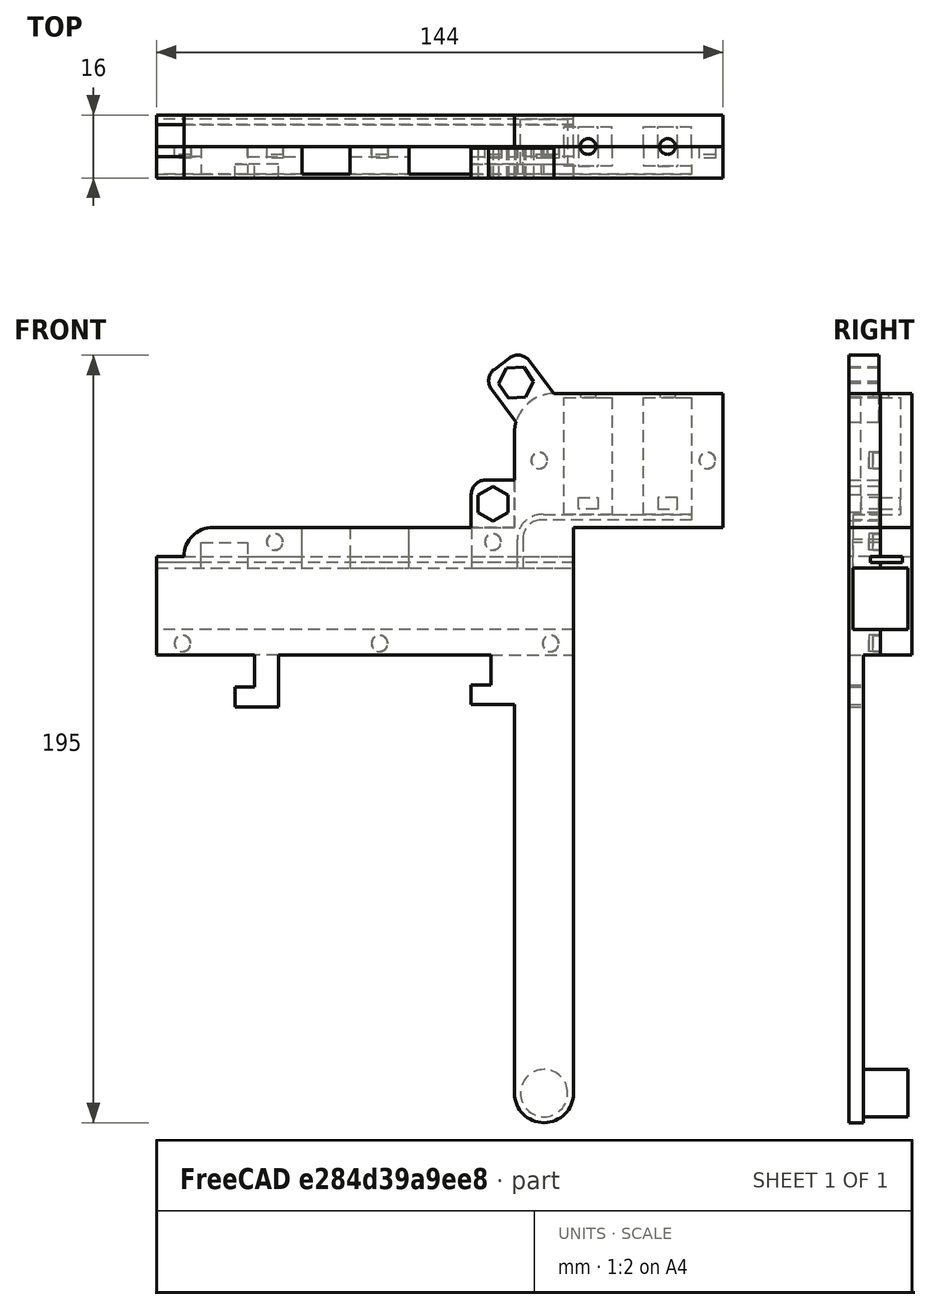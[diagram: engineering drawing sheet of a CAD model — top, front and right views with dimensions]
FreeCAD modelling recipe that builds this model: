
FCSTD DOCUMENT  (FreeCAD 0.19R24276 (Git))
Label: Feeder2
License: All rights reserved
LicenseURL: http://en.wikipedia.org/wiki/All_rights_reserved
objects: PartDesign::SubShapeBinder×35, Sketcher::SketchObject×26, PartDesign::Pocket×18, PartDesign::Pad×14, PartDesign::Hole×7, PartDesign::Body×2, Part::Refine×2, Mesh::Feature×2, Spreadsheet::Sheet×1
note: 143 computed .brp shape members not serialized (recipe doc carries the construction recipe); baked Part::Feature solids carry a one-line shape summary decoded from their .brp

FEATURE [Sketcher::SketchObject] Sketch  label="Base"
  FullyConstrained = false
  MapMode = 3
  Placement = pos=(0,0,0) rot=(1,0,0;1.5708rad)
  sketch-geometry (13):
    g0: LineSegment StartX=14.3949 StartY=7.38 StartZ=0 EndX=91 EndY=7.38 EndZ=0
    g1: LineSegment StartX=91 StartY=7.38 StartZ=0 EndX=91 EndY=31.38 EndZ=0
    g2: LineSegment StartX=0 StartY=-2.16e-14 StartZ=0 EndX=0 EndY=-25.1 EndZ=0
    g3: LineSegment StartX=0 StartY=-25.1 StartZ=0 EndX=106 EndY=-25.1 EndZ=0
    g4: LineSegment StartX=106 StartY=-25.1 StartZ=0 EndX=106 EndY=7.38 EndZ=0
    g5: LineSegment StartX=106 StartY=7.38 StartZ=0 EndX=144 EndY=7.38 EndZ=0
    g6: LineSegment StartX=144 StartY=7.38 StartZ=0 EndX=144 EndY=41.38 EndZ=0
    g7: LineSegment StartX=144 StartY=41.38 StartZ=0 EndX=101 EndY=41.38 EndZ=0
    g8: GeomPoint X=101 Y=31.38 Z=0
    g9: ArcOfCircle CenterX=101 CenterY=31.38 CenterZ=0 NormalX=0 NormalY=0 NormalZ=1 AngleXU=0 Radius=10 StartAngle=1.5708 EndAngle=3.14159
    g10: LineSegment StartX=0 StartY=-2.16e-14 StartZ=0 EndX=7 EndY=-2.16e-14 EndZ=0
    g11: GeomPoint X=14.3949 Y=-0.0149379 Z=0
    g12: ArcOfCircle CenterX=14.3949 CenterY=-0.0149379 CenterZ=0 NormalX=0 NormalY=0 NormalZ=1 AngleXU=0 Radius=7.39494 StartAngle=1.5708 EndAngle=3.13957
  constraints (37):
    c: Horizontal(g0)
    c: Coincident(g1,g0)
    c: Vertical(g1)
    c: Vertical(g2)
    c: Coincident(g3,g2)
    c: Horizontal(g3)
    c: Coincident(g4,g3)
    c: Vertical(g4)
    c: Coincident(g5,g4)
    c: Horizontal(g5)
    c: Coincident(g6,g5)
    c: Vertical(g6)
    c: Vertical(g2,g-1)
    c: Horizontal(g2,g-1)
    c: DistanceY(g2,g2) = 25.1
    c: DistanceX(g3,g3) = 106
    c: DistanceY(g4,g4) = 32.48
    c: DistanceY(g6,g6) = 34
    c: Horizontal(g0,g4)
    c: Coincident(g7,g6)
    c: Horizontal(g7)
    c: DistanceX(g7,g7) = 43
    c: DistanceY(g1,g1) = 24
    c: DistanceX(g0,g4) = 15
    c: Vertical(g8,g7)
    c: Horizontal(g1,g8)
    c: Coincident(g9,g8)
    c: Coincident(g9,g1)
    c: Coincident(g9,g7)
    c: Horizontal(g10)
    c: Horizontal(g10,g2)
    c: Vertical(g10,g2)
    c: DistanceX(g10,g10) = 7
    c: Vertical(g11,g0)
    c: Coincident(g12,g11)
    c: Coincident(g12,g10)
    c: Coincident(g12,g0)
FEATURE [PartDesign::SubShapeBinder] Binder
  BindMode = 0
  ClaimChildren = false
  Context = -> Body001 [Binder.]
  Fuse = false
  MakeFace = true
  PartialLoad = false
  Relative = true
  Support = -> [Sketch]
  _Version = 2
FEATURE [PartDesign::Pad] Pad  label="Left Base"
  Direction = (1,1,1)
  Length = 8
  Length2 = 100
  Profile = -> Binder
  Reversed = true
  Type = 0
FEATURE [Sketcher::SketchObject] Sketch001  label="ReelSupport"
  ExternalGeometry = -> [Binder]
  FullyConstrained = true
  MapMode = 5
  Placement = pos=(0,-8,1.8e-15) rot=(1,0,0;1.5708rad)
  Support = -> [Pad]
  sketch-geometry (5):
    g0: LineSegment StartX=91 StartY=-25.1 StartZ=0 EndX=106 EndY=-25.1 EndZ=0
    g1: LineSegment StartX=106 StartY=-25.1 StartZ=0 EndX=106 EndY=-136.36 EndZ=0
    g2: LineSegment StartX=91 StartY=-136.36 StartZ=0 EndX=91 EndY=-25.1 EndZ=0
    g3: GeomPoint X=98.5 Y=-136.36 Z=0
    g4: ArcOfCircle CenterX=98.5 CenterY=-136.36 CenterZ=0 NormalX=0 NormalY=0 NormalZ=1 AngleXU=0 Radius=7.5 StartAngle=3.14159 EndAngle=6.28319
  constraints (13):
    c: Coincident(g0,g1)
    c: Coincident(g2,g0)
    c: Horizontal(g0)
    c: Vertical(g1)
    c: Vertical(g2)
    c: DistanceX(g0,g0) = 15
    c: DistanceY(g1,g1) = 111.26
    c: Horizontal(g0,g-4)
    c: Vertical(g0,g-4)
    c: Symmetric(g2,g1,g3)
    c: Coincident(g4,g3)
    c: Coincident(g4,g1)
    c: Coincident(g4,g2)
FEATURE [PartDesign::Pad] Pad001  label="Reel Support"
  BaseFeature = -> Pad
  Direction = (1,1,1)
  Length = 3.6
  Length2 = 100
  Profile = -> Sketch001
  Reversed = true
  Type = 0
FEATURE [Sketcher::SketchObject] Sketch002  label="Fix1"
  ExternalGeometry = -> [Sketch001]
  FullyConstrained = true
  MapMode = 5
  Placement = pos=(0,-8,1.8e-15) rot=(1,0,0;1.5708rad)
  Support = -> [Pad001]
  sketch-geometry (6):
    g0: LineSegment StartX=91 StartY=-25.1 StartZ=0 EndX=91 EndY=-37.6 EndZ=0
    g1: LineSegment StartX=91 StartY=-37.6 StartZ=0 EndX=80 EndY=-37.6 EndZ=0
    g2: LineSegment StartX=80 StartY=-37.6 StartZ=0 EndX=80 EndY=-32.6 EndZ=0
    g3: LineSegment StartX=80 StartY=-32.6 StartZ=0 EndX=85 EndY=-32.6 EndZ=0
    g4: LineSegment StartX=85 StartY=-32.6 StartZ=0 EndX=85 EndY=-25.1 EndZ=0
    g5: LineSegment StartX=85 StartY=-25.1 StartZ=0 EndX=91 EndY=-25.1 EndZ=0
  constraints (18):
    c: Vertical(g0)
    c: Coincident(g1,g0)
    c: Horizontal(g1)
    c: Coincident(g2,g1)
    c: Vertical(g2)
    c: Coincident(g3,g2)
    c: Horizontal(g3)
    c: Coincident(g4,g3)
    c: Vertical(g4)
    c: Coincident(g5,g4)
    c: Coincident(g5,g0)
    c: Horizontal(g5)
    c: DistanceY(g2,g2) = 5
    c: DistanceX(g3,g3) = 5
    c: DistanceY(g4,g4) = 7.5
    c: DistanceX(g1,g1) = 11
    c: Horizontal(g0,g-3)
    c: Vertical(g0,g-3)
FEATURE [PartDesign::Pad] Pad002  label="Fix 1"
  BaseFeature = -> Pad001
  Direction = (1,1,1)
  Length = 3.6
  Length2 = 100
  Profile = -> Sketch002
  Reversed = true
  Type = 0
FEATURE [Sketcher::SketchObject] Sketch003  label="Fix2"
  ExternalGeometry = -> [Pad002]
  FullyConstrained = false
  MapMode = 5
  Placement = pos=(0,-8,1.8e-15) rot=(1,0,0;1.5708rad)
  Support = -> [Pad002]
  sketch-geometry (6):
    g0: LineSegment StartX=31 StartY=-38.21 StartZ=0 EndX=20 EndY=-38.21 EndZ=0
    g1: LineSegment StartX=20 StartY=-38.21 StartZ=0 EndX=20 EndY=-33.21 EndZ=0
    g2: LineSegment StartX=20 StartY=-33.21 StartZ=0 EndX=25 EndY=-33.21 EndZ=0
    g3: LineSegment StartX=25 StartY=-33.21 StartZ=0 EndX=25 EndY=-25.1 EndZ=0
    g4: LineSegment StartX=31 StartY=-38.21 StartZ=0 EndX=31 EndY=-25.1 EndZ=0
    g5: LineSegment StartX=31 StartY=-25.1 StartZ=0 EndX=25 EndY=-25.1 EndZ=0
  constraints (18):
    c: Horizontal(g0)
    c: Vertical(g1)
    c: Coincident(g2,g1)
    c: Horizontal(g2)
    c: Coincident(g3,g2)
    c: Vertical(g3)
    c: Coincident(g4,g0)
    c: Vertical(g4)
    c: Coincident(g5,g4)
    c: Coincident(g5,g3)
    c: Horizontal(g5)
    c: Equal(g1,g-3)
    c: Equal(g2,g-4)
    c: Equal(g-5,g0)
    c: Horizontal(g0,g1)
    c: Vertical(g0,g1)
    c: Horizontal(g4,g-6)
    c: DistanceX(g4,g-4) = 54
FEATURE [PartDesign::Pad] Pad003  label="Fix 2"
  BaseFeature = -> Pad002
  Direction = (1,1,1)
  Length = 3.6
  Length2 = 100
  Profile = -> Sketch003
  Reversed = true
  Type = 0
FEATURE [Sketcher::SketchObject] Sketch004  label="Hole1"
  ExternalGeometry = -> [Sketch]
  FullyConstrained = true
  MapMode = 5
  Placement = pos=(0,0,0) rot=(0,0.707107,0.707107;3.14159rad)
  Support = -> [Pad003]
  sketch-geometry (4):
    g0: LineSegment StartX=0 StartY=-2.9 StartZ=0 EndX=-106 EndY=-2.9 EndZ=0
    g1: LineSegment StartX=-106 StartY=-2.9 StartZ=0 EndX=-106 EndY=-18.6 EndZ=0
    g2: LineSegment StartX=-106 StartY=-18.6 StartZ=0 EndX=0 EndY=-18.6 EndZ=0
    g3: LineSegment StartX=0 StartY=-18.6 StartZ=0 EndX=0 EndY=-2.9 EndZ=0
  constraints (12):
    c: Coincident(g0,g1)
    c: Coincident(g1,g2)
    c: Coincident(g2,g3)
    c: Coincident(g3,g0)
    c: Horizontal(g0)
    c: Horizontal(g2)
    c: Vertical(g1)
    c: Vertical(g3)
    c: Vertical(g1,g-3)
    c: Vertical(g2,g-3)
    c: DistanceY(g-3,g1) = 6.5
    c: DistanceY(g1,g0) = 15.7
FEATURE [PartDesign::SubShapeBinder] Binder002
  BindMode = 0
  ClaimChildren = false
  Context = -> Body001 [Binder002.]
  Fuse = false
  MakeFace = true
  PartialLoad = false
  Relative = true
  Support = -> [Sketch004]
  _Version = 2
FEATURE [PartDesign::Pocket] Pocket
  BaseFeature = -> Pad003
  Length = 7
  Length2 = 100
  Profile = -> Binder002
  Type = 0
FEATURE [Sketcher::SketchObject] Sketch005  label="TapeHole"
  ExternalGeometry = -> [Sketch]
  FullyConstrained = true
  MapMode = 5
  Placement = pos=(0,0,0) rot=(1,0,0;1.5708rad)
  Support = -> [XZ_Plane001]
  expr: Constraints[8] = Spreadsheet.tape_heigh
  sketch-geometry (4):
    g0: LineSegment StartX=0 StartY=2.33e-14 StartZ=0 EndX=106 EndY=2.33e-14 EndZ=0
    g1: LineSegment StartX=106 StartY=2.33e-14 StartZ=0 EndX=106 EndY=-1.5 EndZ=0
    g2: LineSegment StartX=106 StartY=-1.5 StartZ=0 EndX=0 EndY=-1.5 EndZ=0
    g3: LineSegment StartX=0 StartY=-1.5 StartZ=0 EndX=0 EndY=2.33e-14 EndZ=0
  constraints (12):
    c: Coincident(g0,g1)
    c: Coincident(g1,g2)
    c: Coincident(g2,g3)
    c: Coincident(g3,g0)
    c: Horizontal(g0)
    c: Horizontal(g2)
    c: Vertical(g1)
    c: Vertical(g3)
    c: DistanceY(g1,g1) = 1.5
    c: Vertical(g0,g-1)
    c: Vertical(g0,g-3)
    c: Horizontal(g0,g-1)
FEATURE [PartDesign::SubShapeBinder] Binder004
  BindMode = 0
  ClaimChildren = false
  Context = -> Body001 [Binder004.]
  Fuse = false
  MakeFace = true
  PartialLoad = false
  Relative = true
  Support = -> [Sketch005]
  _Version = 2
FEATURE [PartDesign::Pocket] Pocket002
  BaseFeature = -> Pocket
  Length = 2.6
  Length2 = 100
  Profile = -> Binder004
  Type = 0
FEATURE [Sketcher::SketchObject] Sketch006  label="BoardHole1"
  ExternalGeometry = -> [Sketch]
  FullyConstrained = true
  MapMode = 5
  Placement = pos=(0,0,0) rot=(1,0,0;1.5708rad)
  Support = -> [XZ_Plane]
  sketch-geometry (4):
    g0: LineSegment StartX=11.4 StartY=3.58 StartZ=0 EndX=23.2 EndY=3.58 EndZ=0
    g1: LineSegment StartX=23.2 StartY=3.58 StartZ=0 EndX=23.2 EndY=-3.42 EndZ=0
    g2: LineSegment StartX=23.2 StartY=-3.42 StartZ=0 EndX=11.4 EndY=-3.42 EndZ=0
    g3: LineSegment StartX=11.4 StartY=-3.42 StartZ=0 EndX=11.4 EndY=3.58 EndZ=0
  constraints (12):
    c: Coincident(g0,g1)
    c: Coincident(g1,g2)
    c: Coincident(g2,g3)
    c: Coincident(g3,g0)
    c: Horizontal(g0)
    c: Horizontal(g2)
    c: Vertical(g1)
    c: Vertical(g3)
    c: DistanceY(g1,g1) = 7
    c: DistanceX(g2,g2) = 11.8
    c: DistanceX(g-1,g0) = 11.4
    c: DistanceY(g0,g-3) = 3.8
FEATURE [PartDesign::SubShapeBinder] Binder006
  BindMode = 0
  ClaimChildren = false
  Context = -> Body001 [Binder006.]
  Fuse = false
  MakeFace = true
  PartialLoad = false
  Relative = true
  Support = -> [Sketch006]
  _Version = 2
FEATURE [PartDesign::Pocket] Pocket004
  BaseFeature = -> Pocket002
  Length = 7
  Length2 = 100
  Profile = -> Binder006
  Type = 0
FEATURE [Sketcher::SketchObject] Sketch007  label="BoardHole2"
  ExternalGeometry = -> [Sketch006,Sketch]
  FullyConstrained = true
  MapMode = 5
  Placement = pos=(0,0,0) rot=(1,0,0;1.5708rad)
  Support = -> [XZ_Plane001]
  sketch-geometry (4):
    g0: LineSegment StartX=37.04 StartY=7.38 StartZ=0 EndX=49.25 EndY=7.38 EndZ=0
    g1: LineSegment StartX=49.25 StartY=7.38 StartZ=0 EndX=49.25 EndY=-3.42 EndZ=0
    g2: LineSegment StartX=49.25 StartY=-3.42 StartZ=0 EndX=37.04 EndY=-3.42 EndZ=0
    g3: LineSegment StartX=37.04 StartY=-3.42 StartZ=0 EndX=37.04 EndY=7.38 EndZ=0
  constraints (12):
    c: Coincident(g0,g1)
    c: Coincident(g1,g2)
    c: Coincident(g2,g3)
    c: Coincident(g3,g0)
    c: Horizontal(g0)
    c: Horizontal(g2)
    c: Vertical(g1)
    c: Vertical(g3)
    c: Horizontal(g0,g-4)
    c: Horizontal(g2,g-3)
    c: DistanceX(g-3,g2) = 13.84
    c: DistanceX(g2,g2) = 12.21
FEATURE [PartDesign::SubShapeBinder] Binder007
  BindMode = 0
  ClaimChildren = false
  Context = -> Body001 [Binder007.]
  Fuse = false
  MakeFace = true
  PartialLoad = false
  Relative = true
  Support = -> [Sketch007]
  _Version = 2
FEATURE [PartDesign::Pocket] Pocket005
  BaseFeature = -> Pocket004
  Length = 7
  Length2 = 100
  Profile = -> Binder007
  Type = 0
FEATURE [Sketcher::SketchObject] Sketch008  label="BoardHole3"
  ExternalGeometry = -> [Sketch,Sketch007]
  FullyConstrained = true
  MapMode = 5
  Placement = pos=(0,0,0) rot=(1,0,0;1.5708rad)
  Support = -> [XZ_Plane001]
  sketch-geometry (4):
    g0: LineSegment StartX=64.22 StartY=7.38 StartZ=0 EndX=80.07 EndY=7.38 EndZ=0
    g1: LineSegment StartX=80.07 StartY=7.38 StartZ=0 EndX=80.07 EndY=-3.42 EndZ=0
    g2: LineSegment StartX=80.07 StartY=-3.42 StartZ=0 EndX=64.22 EndY=-3.42 EndZ=0
    g3: LineSegment StartX=64.22 StartY=-3.42 StartZ=0 EndX=64.22 EndY=7.38 EndZ=0
  constraints (12):
    c: Coincident(g0,g1)
    c: Coincident(g1,g2)
    c: Coincident(g2,g3)
    c: Coincident(g3,g0)
    c: Horizontal(g0)
    c: Horizontal(g2)
    c: Vertical(g1)
    c: Vertical(g3)
    c: Horizontal(g0,g-3)
    c: Horizontal(g2,g-4)
    c: DistanceX(g-4,g2) = 14.97
    c: DistanceX(g2,g2) = 15.85
FEATURE [PartDesign::SubShapeBinder] Binder008
  BindMode = 0
  ClaimChildren = false
  Context = -> Body001 [Binder008.]
  Fuse = false
  MakeFace = true
  PartialLoad = false
  Relative = true
  Support = -> [Sketch008]
  _Version = 2
FEATURE [PartDesign::Pocket] Pocket006
  BaseFeature = -> Pocket005
  Length = 7
  Length2 = 100
  Profile = -> Binder008
  Type = 0
FEATURE [Sketcher::SketchObject] Sketch009  label="MotorHole1"
  ExternalGeometry = -> [Sketch]
  FullyConstrained = true
  MapMode = 5
  Placement = pos=(0,0,0) rot=(1,0,0;1.5708rad)
  Support = -> [XZ_Plane001]
  sketch-geometry (10):
    g0: LineSegment StartX=123.8 StartY=40.41 StartZ=0 EndX=136 EndY=40.41 EndZ=0
    g1: LineSegment StartX=136 StartY=40.41 StartZ=0 EndX=136 EndY=10.7 EndZ=0
    g2: LineSegment StartX=136 StartY=10.7 StartZ=0 EndX=123.8 EndY=10.7 EndZ=0
    g3: LineSegment StartX=123.8 StartY=10.7 StartZ=0 EndX=123.8 EndY=40.41 EndZ=0
    g4: GeomPoint X=129.9 Y=40.41 Z=0
    g5: LineSegment StartX=127.4 StartY=12.01 StartZ=0 EndX=132.4 EndY=12.01 EndZ=0
    g6: LineSegment StartX=132.4 StartY=12.01 StartZ=0 EndX=132.4 EndY=15.01 EndZ=0
    g7: LineSegment StartX=132.4 StartY=15.01 StartZ=0 EndX=127.4 EndY=15.01 EndZ=0
    g8: LineSegment StartX=127.4 StartY=15.01 StartZ=0 EndX=127.4 EndY=12.01 EndZ=0
    g9: GeomPoint X=129.9 Y=15.01 Z=0
  constraints (26):
    c: Coincident(g0,g1)
    c: Coincident(g1,g2)
    c: Coincident(g2,g3)
    c: Coincident(g3,g0)
    c: Horizontal(g0)
    c: Horizontal(g2)
    c: Vertical(g1)
    c: Vertical(g3)
    c: DistanceY(g1,g1) = 29.71
    c: DistanceX(g2,g2) = 12.2
    c: DistanceX(g1,g-3) = 8
    c: DistanceY(g-3,g1) = 3.32
    c: Symmetric(g0,g0,g4)
    c: Coincident(g5,g6)
    c: Coincident(g6,g7)
    c: Coincident(g7,g8)
    c: Coincident(g8,g5)
    c: Horizontal(g5)
    c: Horizontal(g7)
    c: Vertical(g6)
    c: Vertical(g8)
    c: DistanceX(g5,g5) = 5
    c: Symmetric(g7,g7,g9)
    c: DistanceY(g8,g8) = 3
    c: Vertical(g4,g9)
    c: DistanceY(g6,g0) = 25.4
FEATURE [PartDesign::SubShapeBinder] Binder009
  BindMode = 0
  ClaimChildren = false
  Context = -> Body001 [Binder009.]
  Fuse = false
  MakeFace = true
  PartialLoad = false
  Relative = true
  Support = -> [Sketch009]
  _Version = 2
FEATURE [PartDesign::Pocket] Pocket007  label="Motor Hole 1"
  BaseFeature = -> Pocket006
  Length = 5
  Length2 = 100
  Profile = -> Binder009
  Type = 0
FEATURE [Sketcher::SketchObject] Sketch010  label="MotorHole2"
  ExternalGeometry = -> [Sketch009]
  FullyConstrained = true
  MapMode = 5
  Placement = pos=(0,0,0) rot=(1,0,0;1.5708rad)
  Support = -> [XZ_Plane001]
  sketch-geometry (10):
    g0: LineSegment StartX=103.6 StartY=40.41 StartZ=0 EndX=115.8 EndY=40.41 EndZ=0
    g1: LineSegment StartX=115.8 StartY=40.41 StartZ=0 EndX=115.8 EndY=10.7 EndZ=0
    g2: LineSegment StartX=115.8 StartY=10.7 StartZ=0 EndX=103.6 EndY=10.7 EndZ=0
    g3: LineSegment StartX=103.6 StartY=10.7 StartZ=0 EndX=103.6 EndY=40.41 EndZ=0
    g4: GeomPoint X=109.7 Y=40.41 Z=0
    g5: LineSegment StartX=107.2 StartY=15.01 StartZ=0 EndX=112.2 EndY=15.01 EndZ=0
    g6: LineSegment StartX=112.2 StartY=15.01 StartZ=0 EndX=112.2 EndY=12.01 EndZ=0
    g7: LineSegment StartX=112.2 StartY=12.01 StartZ=0 EndX=107.2 EndY=12.01 EndZ=0
    g8: LineSegment StartX=107.2 StartY=12.01 StartZ=0 EndX=107.2 EndY=15.01 EndZ=0
    g9: GeomPoint X=109.7 Y=15.01 Z=0
  constraints (26):
    c: Coincident(g0,g1)
    c: Coincident(g1,g2)
    c: Coincident(g2,g3)
    c: Coincident(g3,g0)
    c: Horizontal(g0)
    c: Horizontal(g2)
    c: Vertical(g1)
    c: Vertical(g3)
    c: Horizontal(g0,g-3)
    c: Horizontal(g1,g-3)
    c: DistanceX(g1,g-3) = 8
    c: Equal(g2,g-4)
    c: Symmetric(g0,g0,g4)
    c: Coincident(g5,g6)
    c: Coincident(g6,g7)
    c: Coincident(g7,g8)
    c: Coincident(g8,g5)
    c: Horizontal(g5)
    c: Horizontal(g7)
    c: Vertical(g6)
    c: Vertical(g8)
    c: Equal(g8,g-6)
    c: Equal(g5,g-5)
    c: Horizontal(g5,g-6)
    c: Symmetric(g5,g5,g9)
    c: Vertical(g9,g4)
FEATURE [PartDesign::SubShapeBinder] Binder010
  BindMode = 0
  ClaimChildren = false
  Context = -> Body001 [Binder010.]
  Fuse = false
  MakeFace = true
  PartialLoad = false
  Relative = true
  Support = -> [Sketch010]
  _Version = 2
FEATURE [PartDesign::Pocket] Pocket008  label="Motor Hole 2"
  BaseFeature = -> Pocket007
  Length = 5
  Length2 = 100
  Profile = -> Binder010
  Type = 0
FEATURE [Sketcher::SketchObject] Sketch011  label="CableMotorHole"
  ExternalGeometry = -> [Sketch009,Sketch008]
  FullyConstrained = false
  MapMode = 5
  Placement = pos=(0,0,0) rot=(1,0,0;1.5708rad)
  Support = -> [XZ_Plane001]
  sketch-geometry (8):
    g0: LineSegment StartX=98.3615 StartY=10.7 StartZ=0 EndX=136 EndY=10.7 EndZ=0
    g1: LineSegment StartX=136 StartY=10.7 StartZ=0 EndX=136 EndY=9.3 EndZ=0
    g2: LineSegment StartX=136 StartY=9.3 StartZ=0 EndX=97.7369 EndY=9.3 EndZ=0
    g3: LineSegment StartX=93.1357 StartY=4.24091 StartZ=0 EndX=93.1357 EndY=-3.42 EndZ=0
    g4: LineSegment StartX=93.1357 StartY=-3.42 StartZ=0 EndX=91.7357 EndY=-3.42 EndZ=0
    g5: LineSegment StartX=91.7357 StartY=-3.42 StartZ=0 EndX=91.7357 EndY=4.24091 EndZ=0
    g6: ArcOfCircle CenterX=98.0352 CenterY=4.40679 CenterZ=0 NormalX=0 NormalY=0 NormalZ=1 AngleXU=0 Radius=4.90229 StartAngle=1.63167 EndAngle=3.17544
    g7: ArcOfCircle CenterX=98.0352 CenterY=4.40679 CenterZ=0 NormalX=0 NormalY=0 NormalZ=1 AngleXU=0 Radius=6.30167 StartAngle=1.51898 EndAngle=3.16792
  constraints (25):
    c: Coincident(g0,g1)
    c: Coincident(g1,g2)
    c: Horizontal(g0)
    c: Horizontal(g2)
    c: Vertical(g1)
    c: DistanceY(g1,g1) = 1.4
    c: Vertical(g0,g-3)
    c: Horizontal(g0,g-3)
    c: Coincident(g3,g4)
    c: Coincident(g4,g5)
    c: Horizontal(g4)
    c: Vertical(g3)
    c: Vertical(g5)
    c: DistanceX(g4,g4) = 1.4
    c: Horizontal(g4,g-4)
    c: Horizontal(g6,g2)
    c: Coincident(g7,g6)
    c: Horizontal(g3,g5)
    c: Horizontal(g7,g0)
    c: Vertical(g7,g0)
    c: Vertical(g6,g2)
    c: Horizontal(g6,g3)
    c: Vertical(g6,g3)
    c: Horizontal(g7,g5)
    c: Vertical(g7,g5)
FEATURE [PartDesign::SubShapeBinder] Binder011
  BindMode = 0
  ClaimChildren = false
  Context = -> Body001 [Binder011.]
  Fuse = false
  MakeFace = true
  PartialLoad = false
  Relative = true
  Support = -> [Sketch011]
  _Version = 2
FEATURE [PartDesign::Pocket] Pocket009  label="Cable Motor Hole"
  BaseFeature = -> Pocket008
  Length = 7
  Length2 = 100
  Profile = -> Binder011
  Type = 0
FEATURE [Sketcher::SketchObject] Sketch012  label="MotorShaftHole1"
  AttachmentOffset = pos=(0,0,22) rot=(0,0,1;0rad)
  FullyConstrained = true
  MapMode = 5
  Placement = pos=(0,0,22) rot=(0,0,1;0rad)
  Support = -> [XY_Plane]
  sketch-geometry (1):
    g0: Circle CenterX=109.7 CenterY=0 CenterZ=0 NormalX=0 NormalY=0 NormalZ=1 AngleXU=0 Radius=2
  constraints (3):
    c: Radius(g0) = 2
    c: Horizontal(g0,g-1)
    c: DistanceX(g-1,g0) = 109.7
FEATURE [PartDesign::SubShapeBinder] Binder015
  BindMode = 0
  ClaimChildren = false
  Context = -> Body001 [Binder015.]
  Fuse = false
  MakeFace = true
  PartialLoad = false
  Relative = true
  Support = -> [Sketch012]
  _Version = 2
FEATURE [PartDesign::Pocket] Pocket013
  BaseFeature = -> Pocket009
  Length = 200
  Length2 = 100
  Profile = -> Binder015
  Reversed = true
  Type = 0
FEATURE [Sketcher::SketchObject] Sketch013  label="MotorShaftHole2"
  AttachmentOffset = pos=(0,0,22) rot=(0,0,1;0rad)
  FullyConstrained = true
  MapMode = 5
  Placement = pos=(0,0,22) rot=(0,0,1;0rad)
  Support = -> [XY_Plane001]
  sketch-geometry (1):
    g0: Circle CenterX=129.9 CenterY=0 CenterZ=0 NormalX=0 NormalY=0 NormalZ=1 AngleXU=0 Radius=2
  constraints (3):
    c: Radius(g0) = 2
    c: Horizontal(g0,g-1)
    c: DistanceX(g-1,g0) = 129.9
FEATURE [PartDesign::SubShapeBinder] Binder016
  BindMode = 0
  ClaimChildren = false
  Context = -> Body001 [Binder016.]
  Fuse = false
  MakeFace = true
  PartialLoad = false
  Relative = true
  Support = -> [Sketch013]
  _Version = 2
FEATURE [PartDesign::Pocket] Pocket014
  BaseFeature = -> Pocket013
  Length = 200
  Length2 = 100
  Profile = -> Binder016
  Reversed = true
  Type = 0
FEATURE [PartDesign::SubShapeBinder] Binder001
  BindMode = 0
  ClaimChildren = false
  Context = -> Body [Binder001.]
  Fuse = false
  MakeFace = true
  PartialLoad = false
  Relative = true
  Support = -> [Sketch]
  _Version = 2
FEATURE [PartDesign::Pad] Pad004  label="Right Main"
  Direction = (1,1,1)
  Length = 8
  Length2 = 100
  Profile = -> Binder001
  Type = 0
  expr: Length = Spreadsheet.tape_width
FEATURE [PartDesign::SubShapeBinder] Binder003
  BindMode = 0
  ClaimChildren = false
  Context = -> Body [Binder003.]
  Fuse = false
  MakeFace = true
  PartialLoad = false
  Relative = true
  Support = -> [Sketch004]
  _Version = 2
FEATURE [PartDesign::Pocket] Pocket001  label="Right Hole 1"
  BaseFeature = -> Pad004
  Length = 7
  Length2 = 100
  Profile = -> Binder003
  Reversed = true
  Type = 0
  expr: Length = Spreadsheet.tape_width - 1
FEATURE [PartDesign::SubShapeBinder] Binder005
  BindMode = 0
  ClaimChildren = false
  Context = -> Body [Binder005.]
  Fuse = false
  MakeFace = true
  PartialLoad = false
  Relative = true
  Support = -> [Sketch005]
  _Version = 2
FEATURE [PartDesign::Pocket] Pocket003  label="Right Tape Hole 1"
  BaseFeature = -> Pocket001
  Length = 5.6
  Length2 = 100
  Profile = -> Binder005
  Reversed = true
  Type = 0
  expr: Length = Spreadsheet.tape_width - 2.6 + 0.2
FEATURE [PartDesign::SubShapeBinder] Binder012
  BindMode = 0
  ClaimChildren = false
  Context = -> Body [Binder012.]
  Fuse = false
  MakeFace = true
  PartialLoad = false
  Relative = true
  Support = -> [Sketch009]
  _Version = 2
FEATURE [PartDesign::SubShapeBinder] Binder013
  BindMode = 0
  ClaimChildren = false
  Context = -> Body [Binder013.]
  Fuse = false
  MakeFace = true
  PartialLoad = false
  Relative = true
  Support = -> [Sketch010]
  _Version = 2
FEATURE [PartDesign::Pocket] Pocket010  label="Right Motor Hole 1"
  BaseFeature = -> Pocket003
  Length = 5
  Length2 = 100
  Profile = -> Binder012
  Reversed = true
  Type = 0
FEATURE [PartDesign::Pocket] Pocket011  label="Right Motor Hole 2"
  BaseFeature = -> Pocket010
  Length = 5
  Length2 = 100
  Profile = -> Binder013
  Reversed = true
  Type = 0
FEATURE [Sketcher::SketchObject] Sketch014  label="MountHole1"
  ExternalGeometry = -> [Sketch006,Sketch007,Sketch]
  FullyConstrained = true
  MapMode = 5
  Placement = pos=(0,0,0) rot=(1,0,0;1.5708rad)
  Support = -> [XZ_Plane]
  sketch-geometry (4):
    g0: LineSegment StartX=0 StartY=0 StartZ=0 EndX=0 EndY=7.38 EndZ=0
    g1: GeomPoint X=0 Y=3.69 Z=0
    g2: LineSegment StartX=23.2 StartY=3.69 StartZ=0 EndX=37.04 EndY=3.69 EndZ=0
    g3: Circle CenterX=30.12 CenterY=3.69 CenterZ=0 NormalX=0 NormalY=0 NormalZ=1 AngleXU=0 Radius=2
  constraints (11):
    c: Vertical(g0)
    c: Horizontal(g0,g-1)
    c: Vertical(g0,g-1)
    c: Horizontal(g0,g-5)
    c: Symmetric(g0,g0,g1)
    c: Horizontal(g2)
    c: Vertical(g2,g-4)
    c: Vertical(g2,g-3)
    c: Horizontal(g1,g2)
    c: Radius(g3) = 2
    c: Symmetric(g2,g2,g3)
FEATURE [Sketcher::SketchObject] Sketch015  label="MountHole2"
  ExternalGeometry = -> [Sketch014,Sketch008,Sketch]
  FullyConstrained = true
  MapMode = 5
  Placement = pos=(0,0,0) rot=(1,0,0;1.5708rad)
  Support = -> [XZ_Plane]
  sketch-geometry (2):
    g0: Circle CenterX=85.535 CenterY=3.69 CenterZ=0 NormalX=0 NormalY=0 NormalZ=1 AngleXU=0 Radius=2
    g1: LineSegment StartX=80.07 StartY=3.69 StartZ=0 EndX=91 EndY=3.69 EndZ=0
  constraints (6):
    c: Equal(g-3,g0)
    c: Horizontal(g-3,g0)
    c: Horizontal(g1)
    c: Vertical(g1,g-4)
    c: Vertical(g1,g-5)
    c: Symmetric(g1,g1,g0)
FEATURE [Sketcher::SketchObject] Sketch016  label="MountHole3"
  ExternalGeometry = -> [Sketch010,Sketch,Sketch015]
  FullyConstrained = true
  MapMode = 5
  Placement = pos=(0,0,0) rot=(1,0,0;1.5708rad)
  Support = -> [XZ_Plane]
  sketch-geometry (3):
    g0: GeomPoint X=144 Y=24.38 Z=0
    g1: LineSegment StartX=91 StartY=24.38 StartZ=0 EndX=103.6 EndY=24.38 EndZ=0
    g2: Circle CenterX=97.3 CenterY=24.38 CenterZ=0 NormalX=0 NormalY=0 NormalZ=1 AngleXU=0 Radius=2
  constraints (7):
    c: Symmetric(g-5,g-5,g0)
    c: Horizontal(g1)
    c: Vertical(g1,g-4)
    c: Vertical(g1,g-3)
    c: Horizontal(g1,g0)
    c: Equal(g2,g-6)
    c: Symmetric(g1,g1,g2)
FEATURE [Sketcher::SketchObject] Sketch017  label="MountHole4"
  ExternalGeometry = -> [Sketch016,Sketch009,Sketch]
  FullyConstrained = true
  MapMode = 5
  Placement = pos=(0,0,0) rot=(1,0,0;1.5708rad)
  Support = -> [XZ_Plane]
  sketch-geometry (2):
    g0: LineSegment StartX=136 StartY=24.38 StartZ=0 EndX=144 EndY=24.38 EndZ=0
    g1: Circle CenterX=140 CenterY=24.38 CenterZ=0 NormalX=0 NormalY=0 NormalZ=1 AngleXU=0 Radius=2
  constraints (6):
    c: Horizontal(g0)
    c: Vertical(g0,g-4)
    c: Vertical(g0,g-5)
    c: Horizontal(g0,g-3)
    c: Equal(g1,g-3)
    c: Symmetric(g0,g0,g1)
FEATURE [Sketcher::SketchObject] Sketch019  label="MountHole6"
  ExternalGeometry = -> [Sketch007,Sketch008]
  FullyConstrained = false
  MapMode = 5
  Placement = pos=(0,0,0) rot=(1,0,0;1.5708rad)
  Support = -> [XZ_Plane]
  sketch-geometry (3):
    g0: Circle CenterX=56.735 CenterY=-22.1 CenterZ=0 NormalX=0 NormalY=0 NormalZ=1 AngleXU=0 Radius=2
    g1: LineSegment StartX=49.25 StartY=7.38 StartZ=0 EndX=64.22 EndY=7.38 EndZ=0
    g2: GeomPoint X=56.735 Y=7.38 Z=0
  constraints (6):
    c: Equal(g0,g-3)
    c: Horizontal(g-3,g0)
    c: Coincident(g1,g-4)
    c: Coincident(g1,g-5)
    c: Symmetric(g1,g1,g2)
    c: Vertical(g0,g2)
FEATURE [Sketcher::SketchObject] Sketch018  label="MountHole5"
  ExternalGeometry = -> [Sketch014,Sketch006,Sketch019]
  FullyConstrained = false
  MapMode = 5
  Placement = pos=(0,0,0) rot=(1,0,0;1.5708rad)
  Support = -> [XZ_Plane]
  sketch-geometry (2):
    g0: Circle CenterX=6.66611 CenterY=-22.1 CenterZ=0 NormalX=0 NormalY=0 NormalZ=1 AngleXU=0 Radius=2
    g1: GeomPoint X=17.3 Y=3.58 Z=0
  constraints (1):
    c: Horizontal(g0,g-5)
FEATURE [Sketcher::SketchObject] Sketch020  label="MountHole7"
  FullyConstrained = false
  MapMode = 5
  Placement = pos=(0,0,0) rot=(1,0,0;1.5708rad)
  Support = -> [XZ_Plane]
  sketch-geometry (1):
    g0: Circle CenterX=100.195 CenterY=-22.1 CenterZ=0 NormalX=0 NormalY=0 NormalZ=1 AngleXU=0 Radius=2
FEATURE [PartDesign::SubShapeBinder] Binder025
  BindMode = 0
  ClaimChildren = false
  Context = -> Body001 [Binder025.]
  Fuse = false
  MakeFace = true
  PartialLoad = false
  Relative = true
  Support = -> [Sketch014]
  _Version = 2
FEATURE [PartDesign::Hole] Hole
  BaseFeature = -> Pocket014
  Depth = 3
  DepthType = 0
  Diameter = 4.2
  DrillForDepth = false
  DrillPoint = 0
  DrillPointAngle = 118
  HoleCutCountersinkAngle = 90
  HoleCutCustomValues = false
  HoleCutDepth = 0
  HoleCutDiameter = 6.1
  HoleCutType = 0
  ModelActualThread = false
  Profile = -> Binder025
  Tapered = false
  TaperedAngle = 90
  ThreadAngle = 0
  ThreadClass = 0
  ThreadCutOffInner = 0
  ThreadCutOffOuter = 0
  ThreadDirection = 0
  ThreadFit = 0
  ThreadPitch = 0
  ThreadSize = 0
  ThreadType = 0
  Threaded = false
FEATURE [PartDesign::SubShapeBinder] Binder026
  BindMode = 0
  ClaimChildren = false
  Context = -> Body [Binder026.]
  Fuse = false
  MakeFace = true
  PartialLoad = false
  Relative = true
  Support = -> [Sketch014]
  _Version = 2
FEATURE [PartDesign::Pad] Pad005
  BaseFeature = -> Pocket011
  Direction = (1,1,1)
  Length = 2
  Length2 = 100
  Profile = -> Binder026
  Reversed = true
  Type = 0
FEATURE [PartDesign::SubShapeBinder] Binder027
  BindMode = 0
  ClaimChildren = false
  Context = -> Body001 [Binder027.]
  Fuse = false
  MakeFace = true
  PartialLoad = false
  Relative = true
  Support = -> [Sketch015]
  _Version = 2
FEATURE [PartDesign::Hole] Hole001
  BaseFeature = -> Hole
  Depth = 3
  DepthType = 0
  Diameter = 4.2
  DrillForDepth = false
  DrillPoint = 0
  DrillPointAngle = 118
  HoleCutCountersinkAngle = 90
  HoleCutCustomValues = false
  HoleCutDepth = 0
  HoleCutDiameter = 6.1
  HoleCutType = 0
  ModelActualThread = false
  Profile = -> Binder027
  Tapered = false
  TaperedAngle = 90
  ThreadAngle = 0
  ThreadClass = 0
  ThreadCutOffInner = 0
  ThreadCutOffOuter = 0
  ThreadDirection = 0
  ThreadFit = 0
  ThreadPitch = 0
  ThreadSize = 0
  ThreadType = 0
  Threaded = false
FEATURE [PartDesign::SubShapeBinder] Binder028
  BindMode = 0
  ClaimChildren = false
  Context = -> Body001 [Binder028.]
  Fuse = false
  MakeFace = true
  PartialLoad = false
  Relative = true
  Support = -> [Sketch016]
  _Version = 2
FEATURE [PartDesign::Hole] Hole002
  BaseFeature = -> Hole001
  Depth = 3
  DepthType = 0
  Diameter = 4.2
  DrillForDepth = false
  DrillPoint = 0
  DrillPointAngle = 118
  HoleCutCountersinkAngle = 90
  HoleCutCustomValues = false
  HoleCutDepth = 0
  HoleCutDiameter = 6.1
  HoleCutType = 0
  ModelActualThread = false
  Profile = -> Binder028
  Tapered = false
  TaperedAngle = 90
  ThreadAngle = 0
  ThreadClass = 0
  ThreadCutOffInner = 0
  ThreadCutOffOuter = 0
  ThreadDirection = 0
  ThreadFit = 0
  ThreadPitch = 0
  ThreadSize = 0
  ThreadType = 0
  Threaded = false
FEATURE [PartDesign::SubShapeBinder] Binder029
  BindMode = 0
  ClaimChildren = false
  Context = -> Body001 [Binder029.]
  Fuse = false
  MakeFace = true
  PartialLoad = false
  Relative = true
  Support = -> [Sketch017]
  _Version = 2
FEATURE [PartDesign::Hole] Hole003
  BaseFeature = -> Hole002
  Depth = 3
  DepthType = 0
  Diameter = 4.2
  DrillForDepth = false
  DrillPoint = 0
  DrillPointAngle = 118
  HoleCutCountersinkAngle = 90
  HoleCutCustomValues = false
  HoleCutDepth = 0
  HoleCutDiameter = 6.1
  HoleCutType = 0
  ModelActualThread = false
  Profile = -> Binder029
  Tapered = false
  TaperedAngle = 90
  ThreadAngle = 0
  ThreadClass = 0
  ThreadCutOffInner = 0
  ThreadCutOffOuter = 0
  ThreadDirection = 0
  ThreadFit = 0
  ThreadPitch = 0
  ThreadSize = 0
  ThreadType = 0
  Threaded = false
FEATURE [PartDesign::SubShapeBinder] Binder030
  BindMode = 0
  ClaimChildren = false
  Context = -> Body001 [Binder030.]
  Fuse = false
  MakeFace = true
  PartialLoad = false
  Relative = true
  Support = -> [Sketch018]
  _Version = 2
FEATURE [PartDesign::Hole] Hole004
  BaseFeature = -> Hole003
  Depth = 3
  DepthType = 0
  Diameter = 4.2
  DrillForDepth = false
  DrillPoint = 0
  DrillPointAngle = 118
  HoleCutCountersinkAngle = 90
  HoleCutCustomValues = false
  HoleCutDepth = 0
  HoleCutDiameter = 6.1
  HoleCutType = 0
  ModelActualThread = false
  Profile = -> Binder030
  Tapered = false
  TaperedAngle = 90
  ThreadAngle = 0
  ThreadClass = 0
  ThreadCutOffInner = 0
  ThreadCutOffOuter = 0
  ThreadDirection = 0
  ThreadFit = 0
  ThreadPitch = 0
  ThreadSize = 0
  ThreadType = 0
  Threaded = false
FEATURE [PartDesign::SubShapeBinder] Binder031
  BindMode = 0
  ClaimChildren = false
  Context = -> Body001 [Binder031.]
  Fuse = false
  MakeFace = true
  PartialLoad = false
  Relative = true
  Support = -> [Sketch019]
  _Version = 2
FEATURE [PartDesign::Hole] Hole005
  BaseFeature = -> Hole004
  Depth = 3
  DepthType = 0
  Diameter = 4.2
  DrillForDepth = false
  DrillPoint = 0
  DrillPointAngle = 118
  HoleCutCountersinkAngle = 90
  HoleCutCustomValues = false
  HoleCutDepth = 0
  HoleCutDiameter = 6.1
  HoleCutType = 0
  ModelActualThread = false
  Profile = -> Binder031
  Tapered = false
  TaperedAngle = 90
  ThreadAngle = 0
  ThreadClass = 0
  ThreadCutOffInner = 0
  ThreadCutOffOuter = 0
  ThreadDirection = 0
  ThreadFit = 0
  ThreadPitch = 0
  ThreadSize = 0
  ThreadType = 0
  Threaded = false
FEATURE [PartDesign::SubShapeBinder] Binder032
  BindMode = 0
  ClaimChildren = false
  Context = -> Body001 [Binder032.]
  Fuse = false
  MakeFace = true
  PartialLoad = false
  Relative = true
  Support = -> [Sketch020]
  _Version = 2
FEATURE [PartDesign::Hole] Hole006
  BaseFeature = -> Hole005
  Depth = 3
  DepthType = 0
  Diameter = 4.2
  DrillForDepth = false
  DrillPoint = 0
  DrillPointAngle = 118
  HoleCutCountersinkAngle = 90
  HoleCutCustomValues = false
  HoleCutDepth = 0
  HoleCutDiameter = 6.1
  HoleCutType = 0
  ModelActualThread = false
  Profile = -> Binder032
  Tapered = false
  TaperedAngle = 90
  ThreadAngle = 0
  ThreadClass = 0
  ThreadCutOffInner = 0
  ThreadCutOffOuter = 0
  ThreadDirection = 0
  ThreadFit = 0
  ThreadPitch = 0
  ThreadSize = 0
  ThreadType = 0
  Threaded = false
FEATURE [PartDesign::SubShapeBinder] Binder033
  BindMode = 0
  ClaimChildren = false
  Context = -> Body [Binder033.]
  Fuse = false
  MakeFace = true
  PartialLoad = false
  Relative = true
  Support = -> [Sketch015]
  _Version = 2
FEATURE [PartDesign::Pad] Pad006
  BaseFeature = -> Pad005
  Direction = (1,1,1)
  Length = 2
  Length2 = 100
  Profile = -> Binder033
  Reversed = true
  Type = 0
FEATURE [PartDesign::SubShapeBinder] Binder034
  BindMode = 0
  ClaimChildren = false
  Context = -> Body [Binder034.]
  Fuse = false
  MakeFace = true
  PartialLoad = false
  Relative = true
  Support = -> [Sketch016]
  _Version = 2
FEATURE [PartDesign::Pad] Pad007
  BaseFeature = -> Pad006
  Direction = (1,1,1)
  Length = 2
  Length2 = 100
  Profile = -> Binder034
  Reversed = true
  Type = 0
FEATURE [PartDesign::SubShapeBinder] Binder035
  BindMode = 0
  ClaimChildren = false
  Context = -> Body [Binder035.]
  Fuse = false
  MakeFace = true
  PartialLoad = false
  Relative = true
  Support = -> [Sketch017]
  _Version = 2
FEATURE [PartDesign::Pad] Pad008
  BaseFeature = -> Pad007
  Direction = (1,1,1)
  Length = 2
  Length2 = 100
  Profile = -> Binder035
  Reversed = true
  Type = 0
FEATURE [PartDesign::SubShapeBinder] Binder036
  BindMode = 0
  ClaimChildren = false
  Context = -> Body [Binder036.]
  Fuse = false
  MakeFace = true
  PartialLoad = false
  Relative = true
  Support = -> [Sketch018]
  _Version = 2
FEATURE [PartDesign::Pad] Pad009
  BaseFeature = -> Pad008
  Direction = (1,1,1)
  Length = 2
  Length2 = 100
  Profile = -> Binder036
  Reversed = true
  Type = 0
FEATURE [PartDesign::SubShapeBinder] Binder037
  BindMode = 0
  ClaimChildren = false
  Context = -> Body [Binder037.]
  Fuse = false
  MakeFace = true
  PartialLoad = false
  Relative = true
  Support = -> [Sketch019]
  _Version = 2
FEATURE [PartDesign::Pad] Pad010
  BaseFeature = -> Pad009
  Direction = (1,1,1)
  Length = 2
  Length2 = 100
  Profile = -> Binder037
  Reversed = true
  Type = 0
FEATURE [PartDesign::SubShapeBinder] Binder038
  BindMode = 0
  ClaimChildren = false
  Context = -> Body [Binder038.]
  Fuse = false
  MakeFace = true
  PartialLoad = false
  Relative = true
  Support = -> [Sketch020]
  _Version = 2
FEATURE [PartDesign::Pad] Pad011
  BaseFeature = -> Pad010
  Direction = (1,1,1)
  Length = 2
  Length2 = 100
  Profile = -> Binder038
  Reversed = true
  Type = 0
FEATURE [PartDesign::SubShapeBinder] Binder041
  BindMode = 0
  ClaimChildren = false
  Context = -> Body [Binder041.]
  Fuse = false
  MakeFace = true
  PartialLoad = false
  Relative = true
  Support = -> [Sketch012]
  _Version = 2
FEATURE [PartDesign::SubShapeBinder] Binder042
  BindMode = 0
  ClaimChildren = false
  Context = -> Body [Binder042.]
  Fuse = false
  MakeFace = true
  PartialLoad = false
  Relative = true
  Support = -> [Sketch013]
  _Version = 2
FEATURE [PartDesign::Pocket] Pocket015
  BaseFeature = -> Pad011
  Length = 200
  Length2 = 100
  Profile = -> Binder041
  Reversed = true
  Type = 0
FEATURE [PartDesign::Pocket] Pocket016
  BaseFeature = -> Pocket015
  Length = 200
  Length2 = 100
  Profile = -> Binder042
  Reversed = true
  Type = 0
FEATURE [Sketcher::SketchObject] Sketch021
  ExternalGeometry = -> [Hole006]
  FullyConstrained = true
  MapMode = 5
  Placement = pos=(0,0,0) rot=(1,0,0;1.5708rad)
  Support = -> [XZ_Plane001]
FEATURE [Sketcher::SketchObject] Sketch022
  ExternalGeometry = -> [Sketch001]
  FullyConstrained = true
  MapMode = 5
  Placement = pos=(0,-4.4,1e-15) rot=(0,0.707107,0.707107;3.14159rad)
  Support = -> [Hole006]
  sketch-geometry (1):
    g0: Circle CenterX=-98.5 CenterY=-136.36 CenterZ=0 NormalX=0 NormalY=0 NormalZ=1 AngleXU=0 Radius=6
  constraints (3):
    c: Radius(g0) = 6
    c: Horizontal(g0,g-3)
    c: Vertical(g0,g-3)
FEATURE [PartDesign::Pad] Pad012
  BaseFeature = -> Hole006
  Direction = (1,1,1)
  Length = 11.4
  Length2 = 100
  Profile = -> Sketch022
  Type = 0
FEATURE [Sketcher::SketchObject] Sketch025
  FullyConstrained = false
  MapMode = 5
  Placement = pos=(0,0,0) rot=(1,0,0;1.5708rad)
  expr: Constraints[9] = Spreadsheet.tape_heigh
  sketch-geometry (4):
    g0: LineSegment StartX=0 StartY=2.33e-14 StartZ=0 EndX=106 EndY=2.33e-14 EndZ=0
    g1: LineSegment StartX=106 StartY=2.33e-14 StartZ=0 EndX=106 EndY=-1.5 EndZ=0
    g2: LineSegment StartX=106 StartY=-1.5 StartZ=0 EndX=0 EndY=-1.5 EndZ=0
    g3: LineSegment StartX=0 StartY=-1.5 StartZ=0 EndX=0 EndY=2.33e-14 EndZ=0
  constraints (10):
    c: Coincident(g0,g1)
    c: Coincident(g1,g2)
    c: Coincident(g2,g3)
    c: Coincident(g3,g0)
    c: Horizontal(g0)
    c: Horizontal(g2)
    c: Vertical(g1)
    c: Vertical(g3)
    c: Horizontal(g0,g-1)
    c: DistanceY(g1,g1) = 1.5
FEATURE [PartDesign::Pocket] Pocket017  label="Right Tape Hole 2"
  BaseFeature = -> Pocket016
  Length = 5
  Length2 = 100
  Profile = -> Sketch025
  Type = 0
  expr: Length = Spreadsheet.tape_width - 3
FEATURE [PartDesign::SubShapeBinder] Binder043
  BindMode = 0
  ClaimChildren = false
  Context = -> Body [Binder043.]
  Fuse = false
  MakeFace = true
  PartialLoad = false
  Relative = true
  Support = -> [Sketch006]
  _Version = 2
FEATURE [PartDesign::SubShapeBinder] Binder044
  BindMode = 0
  ClaimChildren = false
  Context = -> Body [Binder044.]
  Fuse = false
  MakeFace = true
  PartialLoad = false
  Relative = true
  Support = -> [Sketch007]
  _Version = 2
FEATURE [PartDesign::SubShapeBinder] Binder045
  BindMode = 0
  ClaimChildren = false
  Context = -> Body [Binder045.]
  Fuse = false
  MakeFace = true
  PartialLoad = false
  Relative = true
  Support = -> [Sketch008]
  _Version = 2
FEATURE [PartDesign::Body] Body  label="Right"
  Group = -> [Binder001,Pad004,Binder003,Pocket001,Binder005,Pocket003,Binder012,Binder013,Pocket010,Pocket011,Binder026,Pad005,Binder033,Pad006,Binder034,Pad007,Binder035,Pad008,Binder036,Pad009,Binder037,Pad010,Binder038,Pad011,Binder041,Binder042,Pocket015,Pocket016,Sketch025,Pocket017,Binder043,Binder044,Binder045]
  Origin = -> Origin
  Tip = -> Pocket017
FEATURE [Sketcher::SketchObject] Sketch028
  ExternalGeometry = -> [Binder]
  FullyConstrained = false
  MapMode = 5
  Placement = pos=(0,-8,1.8e-15) rot=(1,0,0;1.5708rad)
  Support = -> [Pad012]
  sketch-geometry (27):
    g0: LineSegment StartX=83.597 StartY=19.38 StartZ=0 EndX=91 EndY=19.38 EndZ=0
    g1: LineSegment StartX=91 StartY=19.38 StartZ=0 EndX=91 EndY=7.38 EndZ=0
    g2: LineSegment StartX=91 StartY=7.38 StartZ=0 EndX=80 EndY=7.38 EndZ=0
    g3: LineSegment StartX=80 StartY=7.38 StartZ=0 EndX=80 EndY=15.783 EndZ=0
    g4: ArcOfCircle CenterX=83.597 CenterY=15.783 CenterZ=0 NormalX=0 NormalY=0 NormalZ=1 AngleXU=0 Radius=3.59699 StartAngle=1.5708 EndAngle=3.14159
    g5: GeomPoint X=91 Y=13.38 Z=0
    g6: LineSegment StartX=91 StartY=21.5006 StartZ=0 EndX=80 EndY=21.5006 EndZ=0
    g7: GeomPoint X=85.5 Y=21.5006 Z=0
    g8: GeomPoint X=85.5 Y=13.38 Z=0
    g9: LineSegment StartX=101 StartY=41.38 StartZ=0 EndX=101 EndY=44.38 EndZ=0
    g10: GeomPoint X=95 Y=39.38 Z=0
    g11: LineSegment StartX=101 StartY=31.38 StartZ=0 EndX=91.4 EndY=44.18 EndZ=0
    g12: Circle CenterX=91.4 CenterY=44.18 CenterZ=0 NormalX=0 NormalY=0 NormalZ=1 AngleXU=0 Radius=5
    g13: LineSegment StartX=101 StartY=49.98 StartZ=0 EndX=98.4012 EndY=49.98 EndZ=0
    g14: LineSegment StartX=98.4012 StartY=49.98 StartZ=0 EndX=98.4012 EndY=44.38 EndZ=0
    g15: GeomPoint X=98.4012 Y=49.18 Z=0
    g16: LineSegment StartX=98.4012 StartY=44.38 StartZ=0 EndX=101.012 EndY=44.38 EndZ=0
    g17: LineSegment StartX=98.4012 StartY=49.18 StartZ=0 EndX=91.4 EndY=49.18 EndZ=0
    g18: LineSegment StartX=85.1582 StartY=42.5024 StartZ=0 EndX=91.4 EndY=34.18 EndZ=0
    g19: LineSegment StartX=94.7582 StartY=49.7024 StartZ=0 EndX=101 EndY=41.38 EndZ=0
    g20: LineSegment StartX=91.4 StartY=44.18 StartZ=0 EndX=86.6 EndY=40.58 EndZ=0
    g21: LineSegment StartX=91.4 StartY=44.18 StartZ=0 EndX=96.2 EndY=47.78 EndZ=0
    g22: LineSegment StartX=85.8776 StartY=47.5382 StartZ=0 EndX=89.7224 EndY=50.4218 EndZ=0
    g23: GeomPoint X=87.8 Y=48.98 Z=0
    g24: LineSegment StartX=91.4 StartY=34.18 StartZ=0 EndX=101 EndY=41.38 EndZ=0
    g25: ArcOfCircle CenterX=91.8806 CenterY=47.5442 CenterZ=0 NormalX=0 NormalY=0 NormalZ=1 AngleXU=0 Radius=3.59699 StartAngle=0.643501 EndAngle=2.2143
    g26: ArcOfCircle CenterX=88.0358 CenterY=44.6606 CenterZ=0 NormalX=0 NormalY=0 NormalZ=1 AngleXU=0 Radius=3.59699 StartAngle=2.2143 EndAngle=3.78509
  constraints (68):
    c: Coincident(g0,g1)
    c: Coincident(g1,g2)
    c: Coincident(g2,g3)
    c: Horizontal(g0)
    c: Horizontal(g2)
    c: Vertical(g1)
    c: Vertical(g3)
    c: DistanceX(g2,g2) = 11
    c: Horizontal(g1,g-4)
    c: Vertical(g1,g-4)
    c: Tangent(g0,g4) = 1.5708
    c: Tangent(g3,g4) = 1.5708
    c: DistanceY(g1,g1) = 12
    c: Symmetric(g1,g1,g5)
    c: Horizontal(g6)
    c: Vertical(g6,g0)
    c: Vertical(g6,g3)
    c: Symmetric(g6,g6,g7)
    c: Vertical(g8,g7)
    c: Horizontal(g8,g5)
    c: Vertical(g9)
    c: Horizontal(g9,g-5)
    c: Vertical(g9,g-5)
    c: DistanceY(g9,g9) = 3
    c: PointOnObject(g10,g-6)
    c: Coincident(g11,g-6)
    c: PointOnObject(g10,g11)
    c: Horizontal(g12,g11)
    c: Vertical(g11,g12)
    c: Radius(g12) = 5
    c: Horizontal(g13)
    c: Vertical(g13,g9)
    c: DistanceY(g9,g13) = 5.6
    c: Coincident(g14,g13)
    c: Vertical(g14)
    c: Coincident(g16,g14)
    c: Horizontal(g16)
    c: Coincident(g17,g15)
    c: Horizontal(g17)
    c: Tangent(g12,g17)
    c: Horizontal(g16,g9)
    c: Vertical(g11,g17)
    c: Distance(g11,g10) = 6
    c: Parallel(g18,g11)
    c: Parallel(g19,g11)
    c: Coincident(g20,g11)
    c: Perpendicular(g18,g20)
    c: PointOnObject(g20,g18)
    c: Distance(g20,g11) = 6
    c: PointOnObject(g18,g-6)
    c: Coincident(g21,g11)
    c: Perpendicular(g19,g21)
    c: PointOnObject(g21,g19)
    c: Distance(g21,g11) = 6
    c: PointOnObject(g19,g-6)
    c: Distance(g23,g11) = 6
    c: Coincident(g24,g18)
    c: Coincident(g24,g19)
    c: Equal(g18,g19)
    c: Tangent(g19,g25) = 1.5708
    c: Tangent(g22,g25) = 1.5708
    c: Tangent(g18,g26) = -1.5708
    c: Tangent(g22,g26) = 1.5708
    c: Symmetric(g22,g22,g23)
    c: Parallel(g22,g24)
    c: PointOnObject(g15,g14)
    c: DistanceY(g14,g15) = 4.8
    c: Equal(g4,g26)
FEATURE [PartDesign::Pad] Pad015
  BaseFeature = -> Pad012
  Direction = (1,1,1)
  Length = 7.6
  Length2 = 100
  Profile = -> Sketch028
  Reversed = true
  Type = 0
FEATURE [Sketcher::SketchObject] Sketch029
  ExternalGeometry = -> [Sketch028]
  FullyConstrained = false
  MapMode = 5
  Placement = pos=(0,-0.4,1e-16) rot=(0,0.707107,0.707107;3.14159rad)
  Support = -> [Pad015]
  sketch-geometry (18):
    g0: GeomPoint X=-91 Y=13.38 Z=0
    g1: GeomPoint X=-85.5 Y=7.38 Z=0
    g2: LineSegment StartX=-81.6722 StartY=11.17 StartZ=0 EndX=-81.6722 EndY=15.59 EndZ=0
    g3: LineSegment StartX=-81.6722 StartY=15.59 StartZ=0 EndX=-85.5 EndY=17.8 EndZ=0
    g4: LineSegment StartX=-85.5 StartY=17.8 StartZ=0 EndX=-89.3278 EndY=15.59 EndZ=0
    g5: LineSegment StartX=-89.3278 StartY=15.59 StartZ=0 EndX=-89.3278 EndY=11.17 EndZ=0
    g6: LineSegment StartX=-89.3278 StartY=11.17 StartZ=0 EndX=-85.5 EndY=8.96 EndZ=0
    g7: LineSegment StartX=-85.5 StartY=8.96 StartZ=0 EndX=-81.6722 EndY=11.17 EndZ=0
    g8: Circle CenterX=-85.5 CenterY=13.38 CenterZ=0 NormalX=0 NormalY=0 NormalZ=1 AngleXU=0 Radius=4.42
    g9: GeomPoint X=-87.8 Y=48.98 Z=0
    g10: LineSegment StartX=-89.4353 StartY=40.2207 StartZ=0 EndX=-86.9888 EndY=43.9018 EndZ=0
    g11: LineSegment StartX=-86.9888 StartY=43.9018 StartZ=0 EndX=-88.9535 EndY=47.8612 EndZ=0
    g12: LineSegment StartX=-88.9535 StartY=47.8612 StartZ=0 EndX=-93.3647 EndY=48.1393 EndZ=0
    g13: LineSegment StartX=-93.3647 StartY=48.1393 StartZ=0 EndX=-95.8112 EndY=44.4582 EndZ=0
    g14: LineSegment StartX=-95.8112 StartY=44.4582 StartZ=0 EndX=-93.8465 EndY=40.4988 EndZ=0
    g15: LineSegment StartX=-93.8465 StartY=40.4988 StartZ=0 EndX=-89.4353 EndY=40.2207 EndZ=0
    g16: Circle CenterX=-91.4 CenterY=44.18 CenterZ=0 NormalX=0 NormalY=0 NormalZ=1 AngleXU=0 Radius=4.42
    g17: LineSegment StartX=-87.8 StartY=48.98 StartZ=0 EndX=-91.4 EndY=44.18 EndZ=0
  constraints (38):
    c: Symmetric(g-4,g-4,g1)
    c: Symmetric(g-3,g-3,g0)
    c: Coincident(g2,g3)
    c: Coincident(g3,g4)
    c: Coincident(g4,g5)
    c: Coincident(g5,g6)
    c: Coincident(g6,g7)
    c: Coincident(g7,g2)
    c: Equal(g2, g3-g7) x5
    c: PointOnObject(g2,g8)
    c: PointOnObject(g3,g8)
    c: PointOnObject(g4,g8)
    c: PointOnObject(g5,g8)
    c: PointOnObject(g6,g8)
    c: PointOnObject(g7,g8)
    c: Radius(g8) = 4.42
    c: Vertical(g8,g1)
    c: Horizontal(g8,g0)
    c: Vertical(g3,g1)
    c: Symmetric(g-6,g-6,g9)
    c: Coincident(g10,g11)
    c: Coincident(g11,g12)
    c: Coincident(g12,g13)
    c: Coincident(g13,g14)
    c: Coincident(g14,g15)
    c: Coincident(g15,g10)
    c: Equal(g10, g11-g15) x5
    c: PointOnObject(g10,g16)
    c: PointOnObject(g11,g16)
    c: PointOnObject(g12,g16)
    c: PointOnObject(g13,g16)
    c: PointOnObject(g14,g16)
    c: PointOnObject(g15,g16)
    c: Perpendicular(g17,g-6,g17) = 4.71239
    c: Coincident(g17,g9)
    c: Distance(g17) = 6
    c: Coincident(g16,g17)
    c: Equal(g16,g8)
FEATURE [Spreadsheet::Sheet] Spreadsheet
  cells = A2=Tape Width; B2(tape_width)=8; A3=Board Thickness; B3(board_thickness)=1.62; A4=Tape Heigh; B4(tape_heigh)=1.5; C4=0.6; D4=1; E4=1.2; F4=1.5
FEATURE [PartDesign::Pocket] Pocket018
  BaseFeature = -> Pad015
  Length = 20
  Length2 = 100
  Profile = -> Sketch029
  Type = 0
FEATURE [PartDesign::Body] Body001  label="Left"
  Group = -> [Binder,Pad,Sketch001,Pad001,Sketch002,Pad002,Sketch003,Pad003,Binder002,Pocket,Binder004,Pocket002,Binder006,Pocket004,Binder007,Pocket005,Binder008,Pocket006,Binder009,Pocket007,Binder010,Pocket008,Binder011,Pocket009,Binder015,Pocket013,Binder016,Pocket014,Binder025,Hole,Binder027,Hole001,Binder028,Hole002,Binder029,Hole003,Binder030,Hole004,Binder031,Hole005,Binder032,Hole006,Sketch022,Pad012,+4 more]
  Origin = -> Origin001
  Tip = -> Pocket018
FEATURE [Part::Refine] Body002  label="Right001"
  Source = -> Body
FEATURE [Part::Refine] Body001001  label="Left001"
  Source = -> Body001
FEATURE [Mesh::Feature] Mesh  label="Right001 (Meshed)"
FEATURE [Mesh::Feature] Mesh001  label="Left001 (Meshed)"
